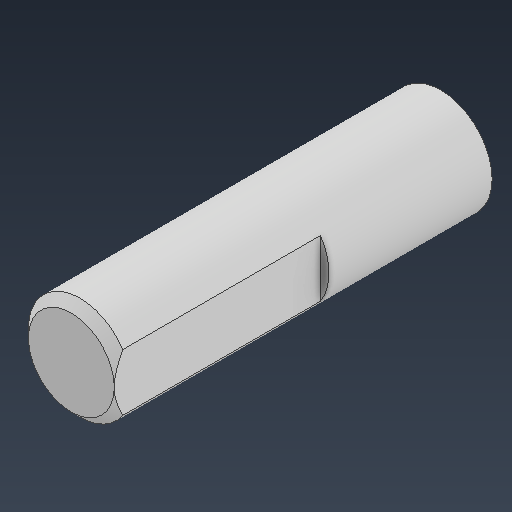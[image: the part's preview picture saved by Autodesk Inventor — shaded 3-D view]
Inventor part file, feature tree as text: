
AUTODESK INVENTOR PART (.ipt)
format: ipt  version: 2021 (Build 250183000, 183)  size: 90,624 bytes
history: native  units: in
note: dims shown in document units (in); Inventor stores cm internally (conversion verified against a paired STEP export)
features: chamfer x1
ambient origin geometry x8: Origin, YZ Plane, XZ Plane, XY Plane, X Axis, Y Axis, Z Axis, Center Point
bodies: Solid1 (feature_tree)
feature tree (1):
  chamfer  "Chamfer1"  [1 undecoded]
note: 1 required parameter value undecoded (feature->parameter linkage not recoverable at this tier; creation-order binding heuristic only, values carry confidence <= 0.55)
